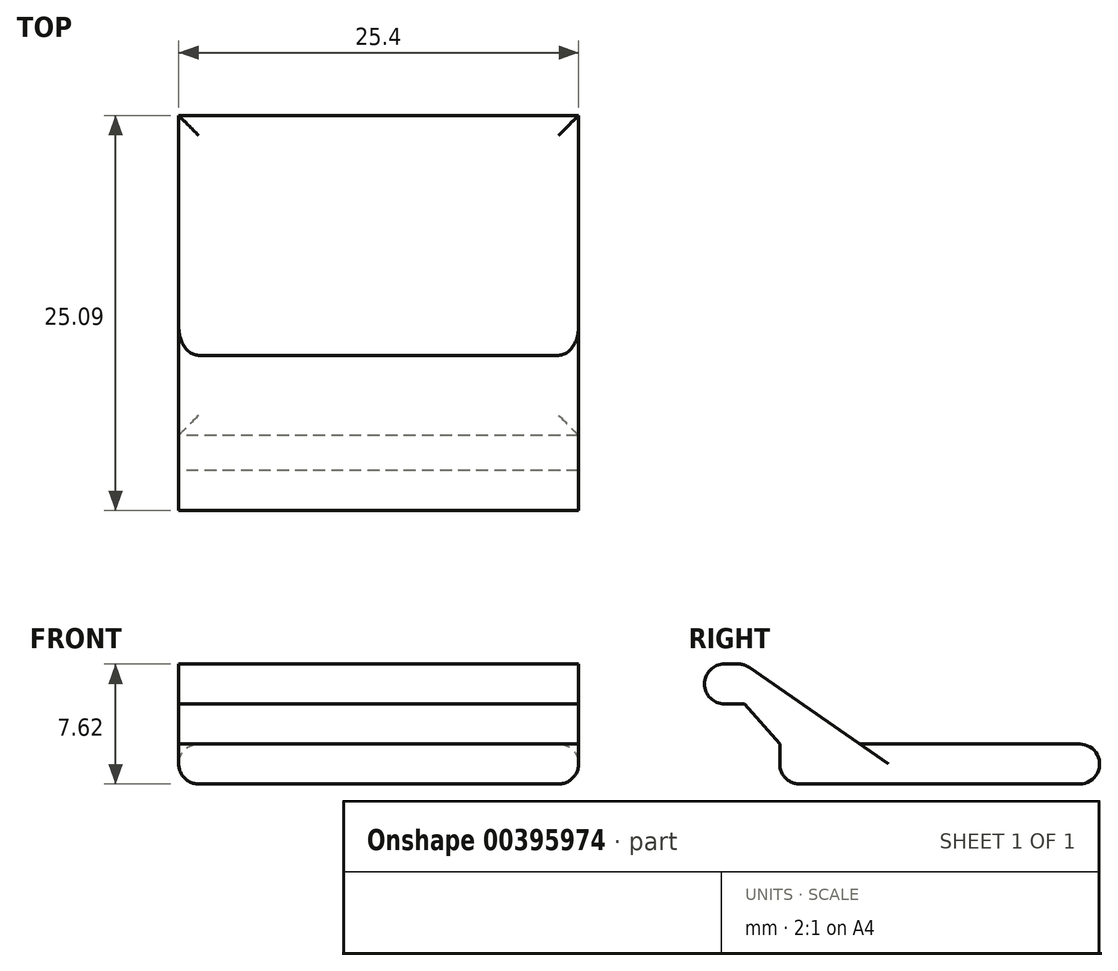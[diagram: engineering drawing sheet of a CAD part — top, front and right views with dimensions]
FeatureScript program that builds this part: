
annotation { "Feature Type Name" : "Feature", "Feature Type Description" : "" }
export const myFeature = defineFeature(function(context is Context, id is Id, definition is map)
    precondition{}
    {
        {
            var Q0;
            Q0=qCreatedBy(makeId("Right.planeOp"),FACE);
            var sketch = newSketch(context, id + "F0", { "sketchPlane" : qUnion([Q0])});
            skLineSegment(sketch, "E0.bottom", {"start": v(-0.63, 1.27) * mm, "end": v(14.6, 1.27) * mm});
            skLineSegment(sketch, "E0.top", {"start": v(-5.72, -1.27) * mm, "end": v(14.6, -1.27) * mm});
            skLineSegment(sketch, "E0.left", {"start": v(-5.72, 1.27) * mm, "end": v(-5.72, -1.27) * mm});
            skLineSegment(sketch, "E0.right", {"start": v(14.6, 1.27) * mm, "end": v(14.6, -1.27) * mm});
            skLineSegment(sketch, "E1", {"start": v(-5.71, 1.27) * mm, "end": v(-7.95, 3.81) * mm});
            skLineSegment(sketch, "E2", {"start": v(-7.95, 3.81) * mm, "end": v(-10.5, 3.81) * mm});
            skLineSegment(sketch, "E3", {"start": v(-10.5, 3.81) * mm, "end": v(-10.5, 6.35) * mm});
            skLineSegment(sketch, "E4", {"start": v(-10.5, 6.35) * mm, "end": v(-7.95, 6.35) * mm});
            skLineSegment(sketch, "E5", {"start": v(-7.95, 6.35) * mm, "end": v(-0.63, 1.27) * mm});
            skSolve(sketch);
        }
        {
            var Q0;
            Q0 = qSketchRegion(id + "F0", true);
            extrude(context, id + "F1", {"entities" : qUnion([Q0]), "depth" : 25.4 * mm});
        }
        {
            var Q0;
            Q0=makeQuery(id+"F1.opExtrude","SWEPT_EDGE",EDGE,{"disambiguationData":[OSD([sQuery(id+"F0.wireOp",EDGE,"E3"),sQuery(id+"F0.wireOp",EDGE,"E4")])]});
            var Q1;
            Q1=makeQuery(id+"F1.opExtrude","SWEPT_EDGE",EDGE,{"disambiguationData":[OSD([sQuery(id+"F0.wireOp",EDGE,"E4"),sQuery(id+"F0.wireOp",EDGE,"E5")])]});
            var Q2;
            Q2=makeQuery(id+"F1.opExtrude","SWEPT_EDGE",EDGE,{"disambiguationData":[OSD([sQuery(id+"F0.wireOp",EDGE,"E2"),sQuery(id+"F0.wireOp",EDGE,"E3")])]});
            var Q3;
            Q3=makeQuery(id+"F1.opExtrude","SWEPT_EDGE",EDGE,{"disambiguationData":[OSD([sQuery(id+"F0.wireOp",EDGE,"E0.bottom"),sQuery(id+"F0.wireOp",EDGE,"E0.right")])]});
            var Q4;
            Q4=makeQuery(id+"F1.opExtrude","SWEPT_EDGE",EDGE,{"disambiguationData":[OSD([sQuery(id+"F0.wireOp",EDGE,"E0.top"),sQuery(id+"F0.wireOp",EDGE,"E0.right")])]});
            var Q5;
            Q5=makeQuery(id+"F1.opExtrude","SWEPT_EDGE",EDGE,{"disambiguationData":[OSD([sQuery(id+"F0.wireOp",EDGE,"E0.top"),sQuery(id+"F0.wireOp",EDGE,"E0.left")])]});
            var Q6;
            Q6=makeQuery(id+"F1.opExtrude","CAP_EDGE",EDGE,{"disambiguationData":[OSD([sQuery(id+"F0.wireOp",EDGE,"E0.bottom")])],"isStart":false});
            var Q7;
            Q7=makeQuery(id+"F1.opExtrude","CAP_EDGE",EDGE,{"disambiguationData":[OSD([sQuery(id+"F0.wireOp",EDGE,"E0.bottom")])],"isStart":true});
            var Q8;
            Q8=makeQuery(id+"F1.opExtrude","CAP_EDGE",EDGE,{"disambiguationData":[OSD([sQuery(id+"F0.wireOp",EDGE,"E0.top")])],"isStart":false});
            var Q9;
            Q9=makeQuery(id+"F1.opExtrude","CAP_EDGE",EDGE,{"disambiguationData":[OSD([sQuery(id+"F0.wireOp",EDGE,"E0.top")])],"isStart":true});
            fillet(context, id + "F2", {"entities" : qUnion([Q0, Q1, Q2, Q3, Q4, Q5, Q6, Q7, Q8, Q9]), "radius" : 1.27 * mm, "tangentPropagation" : true, "allowEdgeOverflow" : false});
        }
    });
